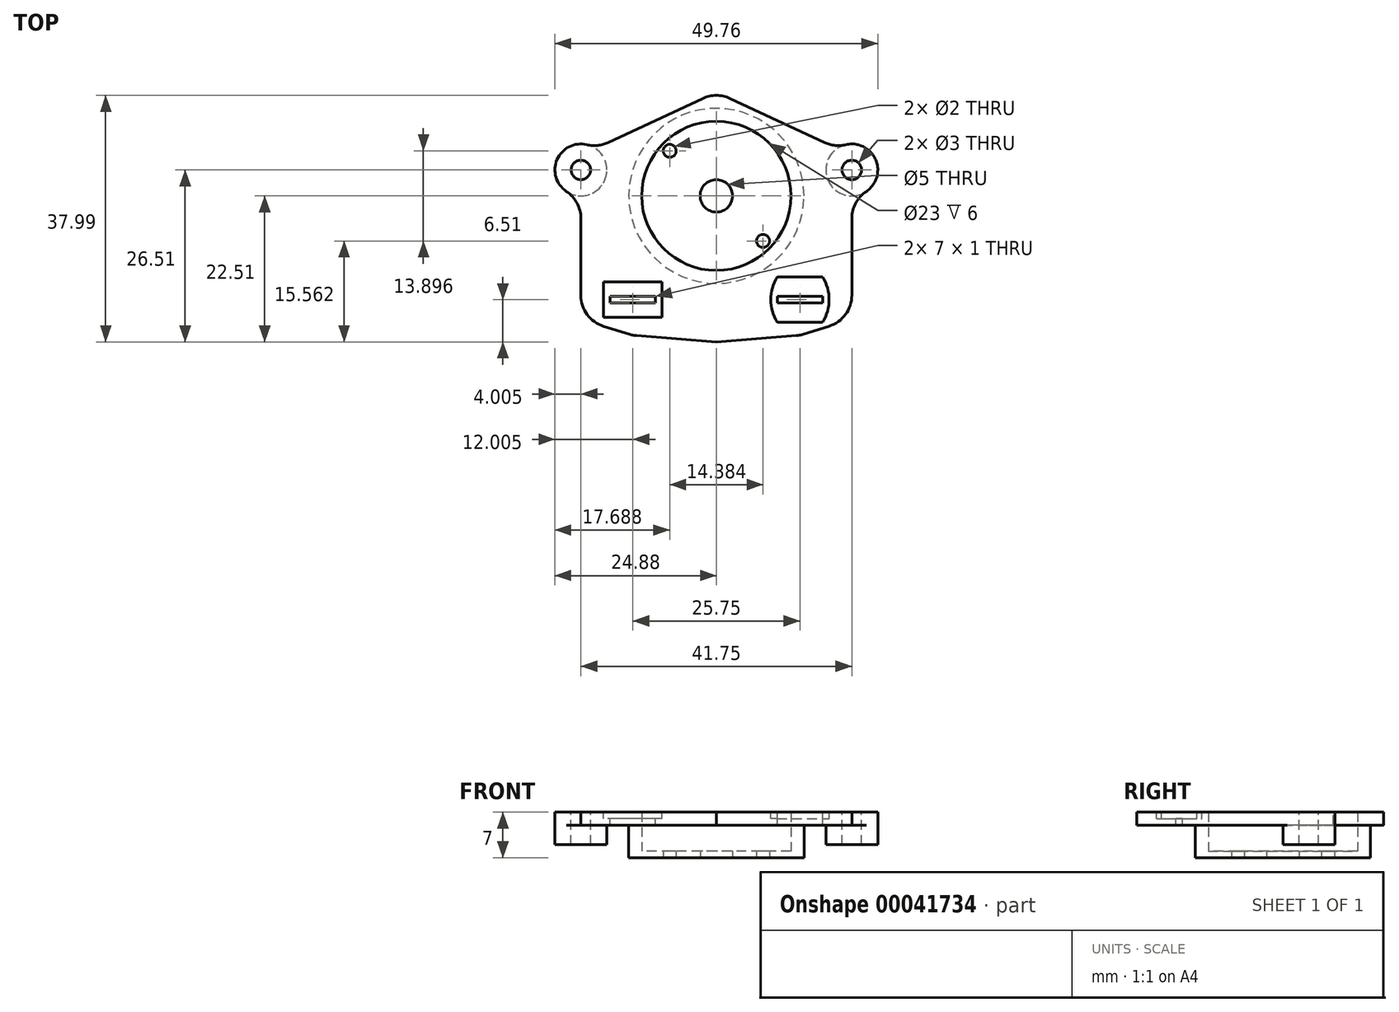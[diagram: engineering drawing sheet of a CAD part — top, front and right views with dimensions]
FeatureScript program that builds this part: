
annotation { "Feature Type Name" : "Feature", "Feature Type Description" : "" }
export const myFeature = defineFeature(function(context is Context, id is Id, definition is map)
    precondition{}
    {
        {
            var Q0;
            Q0=qCreatedBy(makeId("Top.planeOp"),FACE);
            var sketch = newSketch(context, id + "F0", { "sketchPlane" : qUnion([Q0])});
            skCircle(sketch, "E0", {"center": v(0, 0) * mm, "radius": 2.5 * mm});
            skLineSegment(sketch, "E1", {"start": v(-7.2, 6.95) * mm, "end": v(7.2, -6.95) * mm, "construction": true});
            skCircle(sketch, "E2", {"center": v(-7.2, 6.95) * mm, "radius": 1 * mm});
            skCircle(sketch, "E3", {"center": v(7.2, -6.95) * mm, "radius": 1 * mm});
            skCircle(sketch, "E4", {"center": v(0, 0) * mm, "radius": 13.5 * mm});
            skSolve(sketch);
        }
        {
            var Q0;
            Q0=qSketchRegion(id+"F0",true);
            extrude(context, id + "F1", {"entities" : qUnion([Q0]), "depth" : 1 * mm});
        }
        {
            var Q0;
            Q0=makeQuery(id+"F1.opExtrude","CAP_FACE",FACE,{"disambiguationData":[OSD([sQuery(id+"F0.wireOp",EDGE,"E0"),sQuery(id+"F0.wireOp",EDGE,"E2"),sQuery(id+"F0.wireOp",EDGE,"E3"),sQuery(id+"F0.wireOp",EDGE,"E4")])],"isStart":false});
            var sketch = newSketch(context, id + "F2", { "sketchPlane" : qUnion([Q0])});
            skCircle(sketch, "E5", {"center": v(0, 0) * mm, "radius": 13.5 * mm});
            skCircle(sketch, "E6", {"center": v(0, 0) * mm, "radius": 11.5 * mm});
            skLineSegment(sketch, "E7", {"start": v(11.5, 0) * mm, "end": v(13.5, 0) * mm, "construction": true});
            skSolve(sketch);
        }
        {
            var Q0;
            Q0=qSketchRegion(id+"F2",true);
            extrude(context, id + "F3", {"entities" : qUnion([Q0]), "operationType" : NewBodyOperationType.ADD, "depth" : 6 * mm});
        }
        {
            var Q0;
            Q0=makeQuery(id+"F3.opExtrude","CAP_FACE",FACE,{"disambiguationData":[OSD([sQuery(id+"F2.wireOp",EDGE,"E5"),sQuery(id+"F2.wireOp",EDGE,"E6")])],"isStart":false});
            var sketch = newSketch(context, id + "F4", { "sketchPlane" : qUnion([Q0])});
            skLineSegment(sketch, "E8", {"start": v(-20.88, 0) * mm, "end": v(20.88, 0) * mm, "construction": true});
            skCircle(sketch, "E9.0", {"center": v(0, 0) * mm, "radius": 13.5 * mm});
            skLineSegment(sketch, "E10", {"start": v(-20.88, 0) * mm, "end": v(-20.88, 4) * mm, "construction": true});
            skCircle(sketch, "E11", {"center": v(-20.88, 4) * mm, "radius": 1.5 * mm});
            skLineSegment(sketch, "E12", {"start": v(0, 0) * mm, "end": v(0, 16) * mm, "construction": true});
            skCircle(sketch, "E13.MirrorC", {"center": v(20.88, 4) * mm, "radius": 1.5 * mm});
            skLineSegment(sketch, "E14", {"start": v(20.88, 4) * mm, "end": v(20.88, -16) * mm, "construction": true});
            skLineSegment(sketch, "E15", {"start": v(0, 0) * mm, "end": v(0, -22.5) * mm, "construction": true});
            skLineSegment(sketch, "E16", {"start": v(20.88, -16) * mm, "end": v(12.88, -16) * mm, "construction": true});
            skLineSegment(sketch, "E17.rect.bottom", {"start": v(16.38, -16.5) * mm, "end": v(9.38, -16.5) * mm});
            skLineSegment(sketch, "E17.rect.top", {"start": v(16.38, -15.5) * mm, "end": v(9.38, -15.5) * mm});
            skLineSegment(sketch, "E17.rect.left", {"start": v(16.38, -16.5) * mm, "end": v(16.38, -15.5) * mm});
            skLineSegment(sketch, "E17.rect.right", {"start": v(9.38, -16.5) * mm, "end": v(9.38, -15.5) * mm});
            skPoint(sketch, "E17.rect.middle", {"position": v(12.88, -16) * mm});
            skLineSegment(sketch, "E18.MirrorCS", {"start": v(-9.38, -16.5) * mm, "end": v(-9.38, -15.5) * mm});
            skLineSegment(sketch, "E19.MirrorCS", {"start": v(-16.38, -15.5) * mm, "end": v(-9.38, -15.5) * mm});
            skLineSegment(sketch, "E20.MirrorCS", {"start": v(-16.38, -16.5) * mm, "end": v(-9.38, -16.5) * mm});
            skLineSegment(sketch, "E21.MirrorCS", {"start": v(-16.38, -16.5) * mm, "end": v(-16.38, -15.5) * mm});
            skLineSegment(sketch, "E22", {"start": v(12.88, -16) * mm, "end": v(12.88, -21.5) * mm, "construction": true});
            skLineSegment(sketch, "E23", {"start": v(0, -22.5) * mm, "end": v(12.88, -21.5) * mm});
            skLineSegment(sketch, "E24", {"start": v(12.88, -21.5) * mm, "end": v(20.87, -19) * mm});
            skLineSegment(sketch, "E25", {"start": v(20.88, -19) * mm, "end": v(20.88, -21.5) * mm, "construction": true});
            skCircle(sketch, "E26", {"center": v(20.88, 4) * mm, "radius": 4 * mm, "construction": true});
            skLineSegment(sketch, "E27", {"start": v(20.88, -19) * mm, "end": v(20.88, 0) * mm});
            skLineSegment(sketch, "E28", {"start": v(0, 16) * mm, "end": v(18.63, 7.31) * mm});
            skArc(sketch, "E29", {"start": v(20.88, 0) * mm, "mid": v(24.7, 5.17) * mm, "end": v(18.63, 7.31) * mm});
            skLineSegment(sketch, "E30.MirrorCS", {"start": v(0, 16) * mm, "end": v(-18.63, 7.31) * mm});
            skArc(sketch, "E31.MirrorCS", {"start": v(-20.88, 0) * mm, "mid": v(-24.7, 5.17) * mm, "end": v(-18.63, 7.31) * mm});
            skLineSegment(sketch, "E32.MirrorCS", {"start": v(-20.88, -19) * mm, "end": v(-20.88, 0) * mm});
            skLineSegment(sketch, "E33.MirrorCS", {"start": v(-12.88, -21.5) * mm, "end": v(-20.88, -19) * mm});
            skLineSegment(sketch, "E34.MirrorCS", {"start": v(0, -22.5) * mm, "end": v(-12.88, -21.5) * mm});
            skSolve(sketch);
        }
        {
            var Q0;
            Q0=qSketchRegion(id+"F4",true);
            extrude(context, id + "F5", {"entities" : qUnion([Q0]), "operationType" : NewBodyOperationType.ADD, "oppositeDirection" : true, "depth" : 2 * mm});
        }
        {
            var Q0;
            Q0=makeQuery(id+"F5.opExtrude","SWEPT_EDGE",EDGE,{"disambiguationData":[OSD([sQuery(id+"F4.wireOp",EDGE,"E28"),sQuery(id+"F4.wireOp",EDGE,"E30.MirrorCS")])]});
            var Q1;
            Q1=makeQuery(id+"F5.opExtrude","SWEPT_EDGE",EDGE,{"disambiguationData":[OSD([sQuery(id+"F4.wireOp",EDGE,"E24"),sQuery(id+"F4.wireOp",EDGE,"E27")])]});
            var Q2;
            Q2=makeQuery(id+"F5.opExtrude","SWEPT_EDGE",EDGE,{"disambiguationData":[OSD([sQuery(id+"F4.wireOp",EDGE,"E23"),sQuery(id+"F4.wireOp",EDGE,"E24")])]});
            var Q3;
            Q3=makeQuery(id+"F5.opExtrude","SWEPT_EDGE",EDGE,{"disambiguationData":[OSD([sQuery(id+"F4.wireOp",EDGE,"E33.MirrorCS"),sQuery(id+"F4.wireOp",EDGE,"E34.MirrorCS")])]});
            var Q4;
            Q4=makeQuery(id+"F5.opExtrude","SWEPT_EDGE",EDGE,{"disambiguationData":[OSD([sQuery(id+"F4.wireOp",EDGE,"E32.MirrorCS"),sQuery(id+"F4.wireOp",EDGE,"E33.MirrorCS")])]});
            var Q5;
            Q5=makeQuery(id+"F5.opExtrude","SWEPT_EDGE",EDGE,{"disambiguationData":[OSD([sQuery(id+"F4.wireOp",EDGE,"E31.MirrorCS"),sQuery(id+"F4.wireOp",EDGE,"E32.MirrorCS")])]});
            var Q6;
            Q6=makeQuery(id+"F5.opExtrude","SWEPT_EDGE",EDGE,{"disambiguationData":[OSD([sQuery(id+"F4.wireOp",EDGE,"E30.MirrorCS"),sQuery(id+"F4.wireOp",EDGE,"E31.MirrorCS")])]});
            var Q7;
            Q7=makeQuery(id+"F5.opExtrude","SWEPT_EDGE",EDGE,{"disambiguationData":[OSD([sQuery(id+"F4.wireOp",EDGE,"E28"),sQuery(id+"F4.wireOp",EDGE,"E29")])]});
            var Q8;
            Q8=makeQuery(id+"F5.opExtrude","SWEPT_EDGE",EDGE,{"disambiguationData":[OSD([sQuery(id+"F4.wireOp",EDGE,"E27"),sQuery(id+"F4.wireOp",EDGE,"E29")])]});
            fillet(context, id + "F6", {"entities" : qUnion([Q0, Q1, Q2, Q3, Q4, Q5, Q6, Q7, Q8]), "radius" : 5 * mm, "tangentPropagation" : true, "allowEdgeOverflow" : false});
        }
        {
            var Q0;
            Q0=makeQuery(id+"F5.boolean.opBoolean","MERGE",FACE,{"derivedFrom":[makeQuery(id+"F3.opExtrude","CAP_FACE",FACE,{"disambiguationData":[OSD([sQuery(id+"F2.wireOp",EDGE,"E5"),sQuery(id+"F2.wireOp",EDGE,"E6")])],"isStart":false}),makeQuery(id+"F5.opExtrude","CAP_FACE",FACE,{"disambiguationData":[OSD([sQuery(id+"F4.wireOp",EDGE,"E9.0"),sQuery(id+"F4.wireOp",EDGE,"E11"),sQuery(id+"F4.wireOp",EDGE,"E13.MirrorC"),sQuery(id+"F4.wireOp",EDGE,"E17.rect.bottom"),sQuery(id+"F4.wireOp",EDGE,"E17.rect.top"),sQuery(id+"F4.wireOp",EDGE,"E17.rect.left"),sQuery(id+"F4.wireOp",EDGE,"E17.rect.right"),sQuery(id+"F4.wireOp",EDGE,"E18.MirrorCS"),sQuery(id+"F4.wireOp",EDGE,"E19.MirrorCS"),sQuery(id+"F4.wireOp",EDGE,"E20.MirrorCS"),sQuery(id+"F4.wireOp",EDGE,"E21.MirrorCS"),sQuery(id+"F4.wireOp",EDGE,"E23"),sQuery(id+"F4.wireOp",EDGE,"E24"),sQuery(id+"F4.wireOp",EDGE,"E27"),sQuery(id+"F4.wireOp",EDGE,"E28"),sQuery(id+"F4.wireOp",EDGE,"E29"),sQuery(id+"F4.wireOp",EDGE,"E30.MirrorCS"),sQuery(id+"F4.wireOp",EDGE,"E31.MirrorCS"),sQuery(id+"F4.wireOp",EDGE,"E32.MirrorCS"),sQuery(id+"F4.wireOp",EDGE,"E33.MirrorCS"),sQuery(id+"F4.wireOp",EDGE,"E34.MirrorCS")])],"isStart":true})]});
            var sketch = newSketch(context, id + "F7", { "sketchPlane" : qUnion([Q0])});
            skPoint(sketch, "E35.0", {"position": v(12.88, -16) * mm});
            skLineSegment(sketch, "E36.rect.bottom", {"start": v(16.38, -12.5) * mm, "end": v(9.38, -12.5) * mm});
            skLineSegment(sketch, "E36.rect.top", {"start": v(16.38, -19.5) * mm, "end": v(9.38, -19.5) * mm});
            skLineSegment(sketch, "E36.rect.left", {"start": v(16.38, -12.5) * mm, "end": v(16.38, -19.5) * mm});
            skLineSegment(sketch, "E36.rect.right", {"start": v(9.38, -12.5) * mm, "end": v(9.38, -19.5) * mm});
            skLineSegment(sketch, "E37", {"start": v(8.38, -16) * mm, "end": v(17.38, -16) * mm, "construction": true});
            skArc(sketch, "E38", {"start": v(9.38, -12.5) * mm, "mid": v(8.38, -16) * mm, "end": v(9.38, -19.5) * mm});
            skArc(sketch, "E39", {"start": v(16.38, -19.5) * mm, "mid": v(17.38, -16) * mm, "end": v(16.38, -12.5) * mm});
            skPoint(sketch, "E40.MirrorP", {"position": v(-12.88, -16) * mm});
            skLineSegment(sketch, "E41.rect.bottom", {"start": v(-8.38, -18.75) * mm, "end": v(-17.38, -18.75) * mm});
            skLineSegment(sketch, "E41.rect.top", {"start": v(-8.38, -13.25) * mm, "end": v(-17.38, -13.25) * mm});
            skLineSegment(sketch, "E41.rect.left", {"start": v(-8.38, -18.75) * mm, "end": v(-8.38, -13.25) * mm});
            skLineSegment(sketch, "E41.rect.right", {"start": v(-17.38, -18.75) * mm, "end": v(-17.38, -13.25) * mm});
            skSolve(sketch);
        }
        {
            var Q0;
            Q0=qSketchRegion(id+"F7",true);
            extrude(context, id + "F8", {"entities" : qUnion([Q0]), "operationType" : NewBodyOperationType.REMOVE, "oppositeDirection" : true, "depth" : 1 * mm});
        }
        {
            var Q0;
            Q0=makeQuery(id+"F5.opExtrude","CAP_FACE",FACE,{"disambiguationData":[OSD([sQuery(id+"F4.wireOp",EDGE,"E9.0"),sQuery(id+"F4.wireOp",EDGE,"E11"),sQuery(id+"F4.wireOp",EDGE,"E13.MirrorC"),sQuery(id+"F4.wireOp",EDGE,"E17.rect.bottom"),sQuery(id+"F4.wireOp",EDGE,"E17.rect.top"),sQuery(id+"F4.wireOp",EDGE,"E17.rect.left"),sQuery(id+"F4.wireOp",EDGE,"E17.rect.right"),sQuery(id+"F4.wireOp",EDGE,"E18.MirrorCS"),sQuery(id+"F4.wireOp",EDGE,"E19.MirrorCS"),sQuery(id+"F4.wireOp",EDGE,"E20.MirrorCS"),sQuery(id+"F4.wireOp",EDGE,"E21.MirrorCS"),sQuery(id+"F4.wireOp",EDGE,"E23"),sQuery(id+"F4.wireOp",EDGE,"E24"),sQuery(id+"F4.wireOp",EDGE,"E27"),sQuery(id+"F4.wireOp",EDGE,"E28"),sQuery(id+"F4.wireOp",EDGE,"E29"),sQuery(id+"F4.wireOp",EDGE,"E30.MirrorCS"),sQuery(id+"F4.wireOp",EDGE,"E31.MirrorCS"),sQuery(id+"F4.wireOp",EDGE,"E32.MirrorCS"),sQuery(id+"F4.wireOp",EDGE,"E33.MirrorCS"),sQuery(id+"F4.wireOp",EDGE,"E34.MirrorCS")])],"isStart":false});
            var sketch = newSketch(context, id + "F9", { "sketchPlane" : qUnion([Q0])});
            skCircle(sketch, "E42", {"center": v(20.88, -4) * mm, "radius": 4 * mm});
            skCircle(sketch, "E43", {"center": v(20.88, -4) * mm, "radius": 1.5 * mm});
            skCircle(sketch, "E44.MirrorC", {"center": v(-20.88, -4) * mm, "radius": 1.5 * mm});
            skCircle(sketch, "E45.MirrorC", {"center": v(-20.88, -4) * mm, "radius": 4 * mm});
            skSolve(sketch);
        }
        {
            var Q0;
            Q0=qSketchRegion(id+"F9",true);
            extrude(context, id + "F10", {"entities" : qUnion([Q0]), "operationType" : NewBodyOperationType.ADD, "depth" : 3 * mm});
        }
    });
